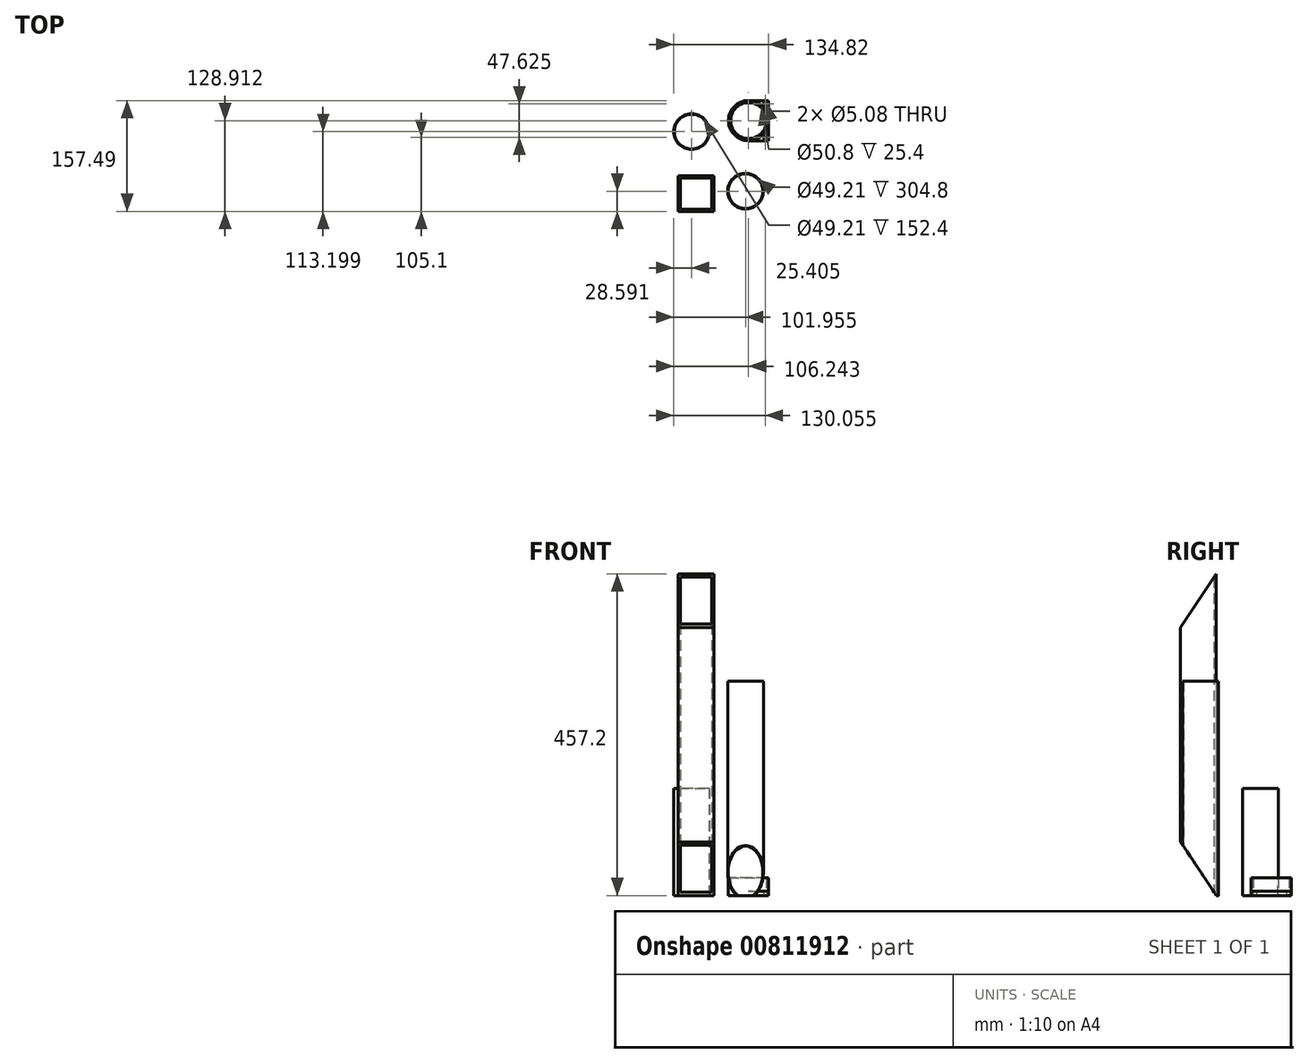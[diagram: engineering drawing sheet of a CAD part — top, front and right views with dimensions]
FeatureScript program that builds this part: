
annotation { "Feature Type Name" : "Feature", "Feature Type Description" : "" }
export const myFeature = defineFeature(function(context is Context, id is Id, definition is map)
    precondition{}
    {
        {
            var Q0;
            Q0=qCreatedBy(makeId("Top.planeOp"),FACE);
            var sketch = newSketch(context, id + "F0", { "sketchPlane" : qUnion([Q0])});
            skCircle(sketch, "E0", {"center": v(-46.05, 48.78) * mm, "radius": 25.4 * mm});
            skCircle(sketch, "E1", {"center": v(-46.05, 48.78) * mm, "radius": 24.6 * mm});
            skSolve(sketch);
        }
        {
            var Q0;
            Q0=makeQuery(id+"F0.imprint","IMPRINT",FACE,{"disambiguationData":[TD([[makeQuery(id+"F0.imprint","IMPRINT",EDGE,{"derivedFrom":sQuery(id+"F0.wireOp",EDGE,"E0")}),1.0]])]});
            extrude(context, id + "F1", {"entities" : qUnion([Q0]), "depth" : 152.4 * mm});
        }
        {
            var Q0;
            Q0=qCreatedBy(makeId("Top.planeOp"),FACE);
            var sketch = newSketch(context, id + "F2", { "sketchPlane" : qUnion([Q0])});
            skCircle(sketch, "E2", {"center": v(30.5, -35.83) * mm, "radius": 25.4 * mm});
            skCircle(sketch, "E3", {"center": v(30.5, -35.83) * mm, "radius": 24.6 * mm});
            skSolve(sketch);
        }
        {
            var Q0;
            Q0=makeQuery(id+"F2.imprint","IMPRINT",FACE,{"disambiguationData":[TD([[makeQuery(id+"F2.imprint","IMPRINT",EDGE,{"derivedFrom":sQuery(id+"F2.wireOp",EDGE,"E2")}),1.0]])]});
            extrude(context, id + "F3", {"entities" : qUnion([Q0]), "depth" : 304.8 * mm});
        }
        {
            var Q0;
            Q0=qCreatedBy(makeId("Top.planeOp"),FACE);
            var sketch = newSketch(context, id + "F4", { "sketchPlane" : qUnion([Q0])});
            skCircle(sketch, "E4", {"center": v(34.8, 64.5) * mm, "radius": 28.58 * mm});
            skLineSegment(sketch, "E5.bottom", {"start": v(34.8, 93.07) * mm, "end": v(63.37, 93.07) * mm});
            skLineSegment(sketch, "E5.top", {"start": v(34.8, 35.92) * mm, "end": v(63.37, 35.92) * mm});
            skLineSegment(sketch, "E5.left", {"start": v(34.8, 93.07) * mm, "end": v(34.8, 35.92) * mm});
            skLineSegment(sketch, "E5.right", {"start": v(63.37, 93.07) * mm, "end": v(63.37, 35.92) * mm});
            skSolve(sketch);
        }
        {
            var Q0;
            {var subQ3=sQuery(id+"F4.wireOp",EDGE,"E5.top");Q0=makeQuery(id+"F4.imprint","IMPRINT",FACE,{"disambiguationData":[TD([[makeQuery(id+"F4.imprint","IMPRINT",EDGE,{"derivedFrom":subQ3}),1.0]])]});}
            var Q1;
            {var subQ0=sQuery(id+"F4.wireOp",EDGE,"E5.left");Q1=makeQuery(id+"F4.imprint","IMPRINT",FACE,{"disambiguationData":[TD([[makeQuery(id+"F4.imprint","IMPRINT",EDGE,{"derivedFrom":subQ0}),1.0]])]});}
            var Q2;
            {var subQ3=sQuery(id+"F4.wireOp",EDGE,"E5.bottom");Q2=makeQuery(id+"F4.imprint","IMPRINT",FACE,{"disambiguationData":[TD([[makeQuery(id+"F4.imprint","IMPRINT",EDGE,{"derivedFrom":subQ3}),-1.0]])]});}
            var Q3;
            {var subQ0=sQuery(id+"F4.wireOp",EDGE,"E5.left");Q3=makeQuery(id+"F4.imprint","IMPRINT",FACE,{"disambiguationData":[TD([[makeQuery(id+"F4.imprint","IMPRINT",EDGE,{"derivedFrom":subQ0}),-1.0]])]});}
            extrude(context, id + "F5", {"entities" : qUnion([Q0, Q1, Q2, Q3]), "depth" : 6.35 * mm});
        }
        {
            var Q0;
            Q0=makeQuery(id+"F5.opExtrude","CAP_FACE",FACE,{"disambiguationData":[OSD([sQuery(id+"F4.wireOp",EDGE,"E4"),sQuery(id+"F4.wireOp",EDGE,"E5.bottom"),sQuery(id+"F4.wireOp",EDGE,"E5.top"),sQuery(id+"F4.wireOp",EDGE,"E5.right")])],"isStart":false});
            var sketch = newSketch(context, id + "F6", { "sketchPlane" : qUnion([Q0])});
            skCircle(sketch, "E6", {"center": v(34.8, 64.5) * mm, "radius": 28.58 * mm});
            skSolve(sketch);
        }
        {
            var Q0;
            {var subQ0=sQuery(id+"F6.wireOp",EDGE,"E6");var subQ3=makeQuery(id+"F6.imprint","INTERSECT",VERTEX,{"derivedFrom":[makeQuery(id+"F5.opExtrude","CAP_EDGE",EDGE,{"disambiguationData":[OSD([sQuery(id+"F4.wireOp",EDGE,"E5.bottom")])],"isStart":false}),subQ0]});Q0=makeQuery(id+"F6.imprint","IMPRINT",FACE,{"disambiguationData":[TD([[makeQuery(id+"F6.imprint","IMPRINT",EDGE,{"disambiguationData":[TD([[subQ3,1.0]])],"derivedFrom":subQ0}),1.0]])]});}
            extrude(context, id + "F7", {"entities" : qUnion([Q0]), "operationType" : NewBodyOperationType.ADD, "depth" : 19.05 * mm});
        }
        {
            var Q0;
            Q0=makeQuery(id+"F5.opExtrude","CAP_FACE",FACE,{"disambiguationData":[OSD([sQuery(id+"F4.wireOp",EDGE,"E4"),sQuery(id+"F4.wireOp",EDGE,"E5.bottom"),sQuery(id+"F4.wireOp",EDGE,"E5.top"),sQuery(id+"F4.wireOp",EDGE,"E5.right")])],"isStart":true});
            var sketch = newSketch(context, id + "F8", { "sketchPlane" : qUnion([Q0])});
            skCircle(sketch, "E7", {"center": v(34.8, -64.5) * mm, "radius": 25.4 * mm});
            skCircle(sketch, "E8", {"center": v(58.6, -88.3) * mm, "radius": 2.54 * mm});
            skCircle(sketch, "E9", {"center": v(58.6, -40.68) * mm, "radius": 2.54 * mm});
            skSolve(sketch);
        }
        {
            var Q0;
            {Q0=qUnion([makeQuery(id+"F8.imprint","IMPRINT",FACE,{"disambiguationData":[TD([[makeQuery(id+"F8.imprint","IMPRINT",EDGE,{"derivedFrom":sQuery(id+"F8.wireOp",EDGE,"E7")}),1.0]])]}),makeQuery(id+"F8.imprint","IMPRINT",FACE,{"disambiguationData":[TD([[makeQuery(id+"F8.imprint","IMPRINT",EDGE,{"derivedFrom":sQuery(id+"F8.wireOp",EDGE,"E8")}),1.0]])]}),makeQuery(id+"F8.imprint","IMPRINT",FACE,{"disambiguationData":[TD([[makeQuery(id+"F8.imprint","IMPRINT",EDGE,{"derivedFrom":sQuery(id+"F8.wireOp",EDGE,"E9")}),1.0]])]})]);}
            extrude(context, id + "F9", {"entities" : qUnion([Q0]), "operationType" : NewBodyOperationType.REMOVE, "endBound" : BoundingType.THROUGH_ALL, "oppositeDirection" : true, "depth" : 25.4 * mm});
        }
        {
            var Q0;
            Q0=qCreatedBy(makeId("Top.planeOp"),FACE);
            var sketch = newSketch(context, id + "F10", { "sketchPlane" : qUnion([Q0])});
            skCircle(sketch, "E10", {"center": v(-46.99, -21.77) * mm, "radius": 26.99 * mm});
            skSolve(sketch);
        }
        {
            var Q0;
            Q0=makeQuery(id+"F10.imprint","IMPRINT",FACE,{"disambiguationData":[TD([[makeQuery(id+"F10.imprint","IMPRINT",EDGE,{"derivedFrom":sQuery(id+"F10.wireOp",EDGE,"E10")}),1.0]])]});
            extrude(context, id + "F11", {"entities" : qUnion([Q0]), "depth" : 6.35 * mm});
        }
        {
            var Q0;
            Q0=makeQuery(id+"F11.opExtrude","CAP_FACE",FACE,{"disambiguationData":[OSD([sQuery(id+"F10.wireOp",EDGE,"E10")])],"isStart":false});
            var sketch = newSketch(context, id + "F12", { "sketchPlane" : qUnion([Q0])});
            skCircle(sketch, "E11", {"center": v(-46.99, -21.77) * mm, "radius": 24.6 * mm});
            skSolve(sketch);
        }
        {
            var Q0;
            Q0=makeQuery(id+"F12.imprint","IMPRINT",FACE,{"disambiguationData":[TD([[makeQuery(id+"F12.imprint","IMPRINT",EDGE,{"derivedFrom":sQuery(id+"F12.wireOp",EDGE,"E11")}),1.0]])]});
            extrude(context, id + "F13", {"entities" : qUnion([Q0]), "operationType" : NewBodyOperationType.ADD, "depth" : 19.05 * mm});
        }
        {
            var Q0;
            Q0=makeQuery(id+"F11.opExtrude","CAP_FACE",FACE,{"disambiguationData":[OSD([sQuery(id+"F10.wireOp",EDGE,"E10")])],"isStart":true});
            var sketch = newSketch(context, id + "F14", { "sketchPlane" : qUnion([Q0])});
            skCircle(sketch, "E12", {"center": v(-46.99, 21.77) * mm, "radius": 21.59 * mm, "construction": true});
            skCircle(sketch, "E13", {"center": v(-46.99, 43.36) * mm, "radius": 2.16 * mm});
            skCircle(sketch, "E14", {"center": v(-25.4, 21.77) * mm, "radius": 2.16 * mm});
            skCircle(sketch, "E15", {"center": v(-46.99, 0.18) * mm, "radius": 2.16 * mm});
            skCircle(sketch, "E16", {"center": v(-68.58, 21.77) * mm, "radius": 2.16 * mm});
            skCircle(sketch, "E17", {"center": v(-46.99, 21.77) * mm, "radius": 12.7 * mm});
            skSolve(sketch);
        }
        {
            var Q0;
            {Q0=qUnion([makeQuery(id+"F14.imprint","IMPRINT",FACE,{"disambiguationData":[TD([[makeQuery(id+"F14.imprint","IMPRINT",EDGE,{"derivedFrom":sQuery(id+"F14.wireOp",EDGE,"E13")}),1.0]])]}),makeQuery(id+"F14.imprint","IMPRINT",FACE,{"disambiguationData":[TD([[makeQuery(id+"F14.imprint","IMPRINT",EDGE,{"derivedFrom":sQuery(id+"F14.wireOp",EDGE,"E14")}),1.0]])]}),makeQuery(id+"F14.imprint","IMPRINT",FACE,{"disambiguationData":[TD([[makeQuery(id+"F14.imprint","IMPRINT",EDGE,{"derivedFrom":sQuery(id+"F14.wireOp",EDGE,"E15")}),1.0]])]}),makeQuery(id+"F14.imprint","IMPRINT",FACE,{"disambiguationData":[TD([[makeQuery(id+"F14.imprint","IMPRINT",EDGE,{"derivedFrom":sQuery(id+"F14.wireOp",EDGE,"E16")}),1.0]])]}),makeQuery(id+"F14.imprint","IMPRINT",FACE,{"disambiguationData":[TD([[makeQuery(id+"F14.imprint","IMPRINT",EDGE,{"derivedFrom":sQuery(id+"F14.wireOp",EDGE,"E17")}),1.0]])]})]);}
            var Q1;
            Q1=makeQuery(id+"F13.opExtrude","CAP_FACE",FACE,{"disambiguationData":[OSD([sQuery(id+"F12.wireOp",EDGE,"E11")])],"isStart":false});
            extrude(context, id + "F15", {"entities" : qUnion([Q0, Q1]), "operationType" : NewBodyOperationType.REMOVE, "endBound" : BoundingType.THROUGH_ALL, "oppositeDirection" : true, "depth" : 25.4 * mm});
        }
        {
            var Q0;
            Q0=makeQuery(id+"F13.opExtrude","CAP_FACE",FACE,{"disambiguationData":[OSD([sQuery(id+"F12.wireOp",EDGE,"E11")])],"isStart":false});
            var sketch = newSketch(context, id + "F16", { "sketchPlane" : qUnion([Q0])});
            skArc(sketch, "E18", {"start": v(-51.63, -1.23) * mm, "mid": v(-46.99, -4.94) * mm, "end": v(-42.34, -1.23) * mm});
            skArc(sketch, "E19", {"start": v(-26.45, -17.13) * mm, "mid": v(-30.16, -21.77) * mm, "end": v(-26.45, -26.42) * mm});
            skArc(sketch, "E20", {"start": v(-42.34, -42.31) * mm, "mid": v(-46.99, -38.6) * mm, "end": v(-51.63, -42.31) * mm});
            skArc(sketch, "E21", {"start": v(-67.53, -26.42) * mm, "mid": v(-63.81, -21.77) * mm, "end": v(-67.53, -17.13) * mm});
            skLineSegment(sketch, "E22", {"start": v(-52.41, 2.23) * mm, "end": v(-51.63, -1.23) * mm});
            skLineSegment(sketch, "E23", {"start": v(-41.56, 2.23) * mm, "end": v(-42.34, -1.23) * mm});
            skLineSegment(sketch, "E24", {"start": v(-70.99, -16.34) * mm, "end": v(-67.53, -17.13) * mm});
            skLineSegment(sketch, "E25", {"start": v(-22.99, -16.34) * mm, "end": v(-26.45, -17.13) * mm});
            skLineSegment(sketch, "E26.trimOffspring", {"start": v(-42.34, -42.31) * mm, "end": v(-41.56, -45.77) * mm});
            skLineSegment(sketch, "E27.trimOffspring", {"start": v(-51.63, -42.31) * mm, "end": v(-52.41, -45.77) * mm});
            skLineSegment(sketch, "E28.trimOffspring", {"start": v(-26.45, -26.42) * mm, "end": v(-22.99, -27.2) * mm});
            skLineSegment(sketch, "E29.trimOffspring", {"start": v(-67.53, -26.42) * mm, "end": v(-70.99, -27.2) * mm});
            skArc(sketch, "E30.0", {"start": v(-70.99, -16.34) * mm, "mid": v(-71.6, -21.77) * mm, "end": v(-70.99, -27.2) * mm});
            skArc(sketch, "E31.trimOffspring", {"start": v(-41.56, 2.23) * mm, "mid": v(-46.99, 2.83) * mm, "end": v(-52.41, 2.23) * mm});
            skArc(sketch, "E32.trimOffspring", {"start": v(-22.99, -27.2) * mm, "mid": v(-22.38, -21.77) * mm, "end": v(-22.99, -16.34) * mm});
            skArc(sketch, "E33.trimOffspring", {"start": v(-52.41, -45.77) * mm, "mid": v(-46.99, -46.38) * mm, "end": v(-41.56, -45.77) * mm});
            skSolve(sketch);
        }
        {
            var Q0;
            {Q0=qUnion([makeQuery(id+"F16.imprint","IMPRINT",FACE,{"disambiguationData":[TD([[makeQuery(id+"F16.imprint","IMPRINT",EDGE,{"derivedFrom":sQuery(id+"F16.wireOp",EDGE,"E18")}),1.0]])]}),makeQuery(id+"F16.imprint","IMPRINT",FACE,{"disambiguationData":[TD([[makeQuery(id+"F16.imprint","IMPRINT",EDGE,{"derivedFrom":sQuery(id+"F16.wireOp",EDGE,"E19")}),1.0]])]}),makeQuery(id+"F16.imprint","IMPRINT",FACE,{"disambiguationData":[TD([[makeQuery(id+"F16.imprint","IMPRINT",EDGE,{"derivedFrom":sQuery(id+"F16.wireOp",EDGE,"E20")}),1.0]])]}),makeQuery(id+"F16.imprint","IMPRINT",FACE,{"disambiguationData":[TD([[makeQuery(id+"F16.imprint","IMPRINT",EDGE,{"derivedFrom":sQuery(id+"F16.wireOp",EDGE,"E21")}),1.0]])]})]);}
            extrude(context, id + "F17", {"entities" : qUnion([Q0]), "operationType" : NewBodyOperationType.REMOVE, "oppositeDirection" : true, "depth" : 19.05 * mm});
        }
        {
            var Q0;
            Q0=makeQuery(id+"F13.opExtrude","CAP_FACE",FACE,{"disambiguationData":[OSD([sQuery(id+"F12.wireOp",EDGE,"E11")])],"isStart":false});
            var sketch = newSketch(context, id + "F18", { "sketchPlane" : qUnion([Q0])});
            skArc(sketch, "E34.0", {"start": v(-54.25, -0.94) * mm, "mid": v(-46.99, -7.48) * mm, "end": v(-39.72, -0.94) * mm});
            skArc(sketch, "E34.1", {"start": v(-26.15, -14.5) * mm, "mid": v(-31.38, -6.17) * mm, "end": v(-39.72, -0.94) * mm});
            skArc(sketch, "E34.2", {"start": v(-26.15, -14.5) * mm, "mid": v(-32.7, -21.77) * mm, "end": v(-26.15, -29.04) * mm});
            skArc(sketch, "E34.3", {"start": v(-39.72, -42.6) * mm, "mid": v(-31.38, -37.38) * mm, "end": v(-26.15, -29.04) * mm});
            skArc(sketch, "E34.4", {"start": v(-39.72, -42.6) * mm, "mid": v(-46.99, -36.06) * mm, "end": v(-54.25, -42.6) * mm});
            skArc(sketch, "E34.5", {"start": v(-54.25, -0.94) * mm, "mid": v(-62.59, -6.17) * mm, "end": v(-67.82, -14.5) * mm});
            skArc(sketch, "E34.6", {"start": v(-67.82, -29.04) * mm, "mid": v(-62.59, -37.38) * mm, "end": v(-54.25, -42.6) * mm});
            skArc(sketch, "E34.7", {"start": v(-67.82, -29.04) * mm, "mid": v(-61.27, -21.77) * mm, "end": v(-67.82, -14.5) * mm});
            skLineSegment(sketch, "E35.5", {"start": v(-47.48, 9.18) * mm, "end": v(-46.99, 7.01) * mm});
            skLineSegment(sketch, "E35.11", {"start": v(-46.5, 9.18) * mm, "end": v(-46.99, 7.01) * mm});
            skSolve(sketch);
        }
        {
            var Q0;
            Q0=makeQuery(id+"F18.imprint","IMPRINT",FACE,{"disambiguationData":[TD([[makeQuery(id+"F18.imprint","IMPRINT",EDGE,{"derivedFrom":sQuery(id+"F18.wireOp",EDGE,"E34.0")}),-1.0]])]});
            extrude(context, id + "F19", {"entities" : qUnion([Q0]), "operationType" : NewBodyOperationType.REMOVE, "oppositeDirection" : true, "depth" : 19.05 * mm});
        }
        {
            var Q0;
            Q0=makeQuery(id+"F11.opExtrude","CAP_FACE",FACE,{"disambiguationData":[OSD([sQuery(id+"F10.wireOp",EDGE,"E10")])],"isStart":true});
            var sketch = newSketch(context, id + "F20", { "sketchPlane" : qUnion([Q0])});
            skCircle(sketch, "E36", {"center": v(-46.99, 21.77) * mm, "radius": 25.4 * mm});
            skSolve(sketch);
        }
        {
            var Q0;
            Q0=makeQuery(id+"F20.imprint","IMPRINT",FACE,{"disambiguationData":[TD([[makeQuery(id+"F20.imprint","IMPRINT",EDGE,{"derivedFrom":sQuery(id+"F20.wireOp",EDGE,"E36")}),1.0]])]});
            extrude(context, id + "F21", {"entities" : qUnion([Q0]), "operationType" : NewBodyOperationType.REMOVE, "oppositeDirection" : true, "depth" : 3.17 * mm});
        }
        {
            var Q0;
            Q0=makeQuery(id+"F11.opExtrude","SWEPT_BODY",BODY,{"disambiguationData":[OSD([sQuery(id+"F10.wireOp",EDGE,"E10")])]});
            deleteBodies(context, id + "F22", {"entities" : qUnion([Q0])});
        }
        {
            var Q0;
            Q0=qCreatedBy(makeId("Top.planeOp"),FACE);
            var sketch = newSketch(context, id + "F23", { "sketchPlane" : qUnion([Q0])});
            skLineSegment(sketch, "E37.bottom", {"start": v(-64.95, -13.62) * mm, "end": v(-14.15, -13.62) * mm});
            skLineSegment(sketch, "E37.top", {"start": v(-64.95, -64.42) * mm, "end": v(-14.15, -64.42) * mm});
            skLineSegment(sketch, "E37.left", {"start": v(-64.95, -13.62) * mm, "end": v(-64.95, -64.42) * mm});
            skLineSegment(sketch, "E37.right", {"start": v(-14.15, -13.62) * mm, "end": v(-14.15, -64.42) * mm});
            skLineSegment(sketch, "E38.bottom", {"start": v(-61.77, -16.8) * mm, "end": v(-17.32, -16.8) * mm});
            skLineSegment(sketch, "E38.top", {"start": v(-61.77, -61.25) * mm, "end": v(-17.32, -61.25) * mm});
            skLineSegment(sketch, "E38.left", {"start": v(-61.77, -16.8) * mm, "end": v(-61.77, -61.25) * mm});
            skLineSegment(sketch, "E38.right", {"start": v(-17.32, -16.8) * mm, "end": v(-17.32, -61.25) * mm});
            skSolve(sketch);
        }
        {
            var Q0;
            Q0=makeQuery(id+"F23.imprint","IMPRINT",FACE,{"disambiguationData":[TD([[makeQuery(id+"F23.imprint","IMPRINT",EDGE,{"derivedFrom":sQuery(id+"F23.wireOp",EDGE,"E37.bottom")}),-1.0]])]});
            extrude(context, id + "F24", {"entities" : qUnion([Q0]), "depth" : 457.2 * mm});
        }
        {
            var Q0;
            Q0=makeQuery(id+"F24.opExtrude","SWEPT_FACE",FACE,{"disambiguationData":[OSD([sQuery(id+"F23.wireOp",EDGE,"E37.left")])]});
            var sketch = newSketch(context, id + "F25", { "sketchPlane" : qUnion([Q0])});
            skLineSegment(sketch, "E39", {"start": v(64.42, 457.2) * mm, "end": v(64.42, 381) * mm});
            skLineSegment(sketch, "E40", {"start": v(64.42, 381) * mm, "end": v(13.62, 457.2) * mm});
            skLineSegment(sketch, "E41", {"start": v(13.62, 457.2) * mm, "end": v(64.42, 457.2) * mm});
            skLineSegment(sketch, "E42", {"start": v(64.42, 76.2) * mm, "end": v(64.42, 0) * mm});
            skLineSegment(sketch, "E43", {"start": v(64.42, 0) * mm, "end": v(13.62, 0) * mm});
            skLineSegment(sketch, "E44", {"start": v(13.62, 0) * mm, "end": v(64.42, 76.2) * mm});
            skSolve(sketch);
        }
        {
            var Q0;
            {Q0=qUnion([makeQuery(id+"F25.imprint","IMPRINT",FACE,{"disambiguationData":[TD([[makeQuery(id+"F25.imprint","IMPRINT",EDGE,{"derivedFrom":sQuery(id+"F25.wireOp",EDGE,"E39")}),-1.0]])]}),makeQuery(id+"F25.imprint","IMPRINT",FACE,{"disambiguationData":[TD([[makeQuery(id+"F25.imprint","IMPRINT",EDGE,{"derivedFrom":sQuery(id+"F25.wireOp",EDGE,"E42")}),-1.0]])]})]);}
            extrude(context, id + "F26", {"entities" : qUnion([Q0]), "operationType" : NewBodyOperationType.REMOVE, "endBound" : BoundingType.THROUGH_ALL, "oppositeDirection" : true, "depth" : 25.4 * mm});
        }
    });
